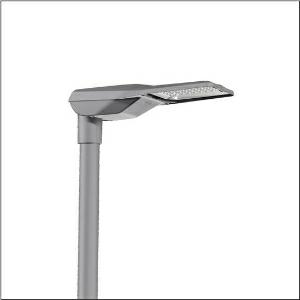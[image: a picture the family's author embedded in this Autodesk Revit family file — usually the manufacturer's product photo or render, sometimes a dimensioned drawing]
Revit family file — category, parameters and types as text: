
# Revit family: streetlight_sl_21_iq_mini___st0_8a_5xe2c41d08hb_7f29
name_source: partatom
category: Lighting Fixtures
units: mm (PartAtom-declared; Revit-internal decimal feet)

## family parameters
Cut with Voids When Loaded = No
Host = Face
Light Source = No
Part Type = Normal
Room Calculation Point = No
Round Connector Dimension = Use Diameter
Shared = No

## types (1)
- --- (1 x LED, 9860 lm, 70.9 W, 4000K)
    Apparent Load = 71 VA
    CIE Flux Codes = 38 75 97 100 100
    Color Rendering = 70
    Color Temperature = 4000K
    Default Elevation = 1800 mm
    Description = Streetlight SL 21 iQ mini, mast luminaire, primary light control with lens, of PMMA, primary optical cover: cover, of toughened safety glass, transparent, light distribution: ST0.8a, light emission: direct distribution, primary light characteristic: asymmetric, installation type: post-top, side-entry, LED, High Power LED, rated luminous flux: 9.860lm, luminous efficacy: 139lm/W, light colour: 740, colour temperature: 4000K, control gear: iQ-Comfort, control: Auto-Match, Temp-Guard, Lumen-Switch, Night-Set, Smart-Wire, Light-Fading, Desk-Remote (wireless, voltage-free reading and setting of iQ features in the workshop via application-optimized NFC function/RFID function), optimised constant luminous flux control (CLO 2.0), pre-setting: linear dimming characteristic, mains connection: 220..240V, AC, 50/60Hz, start of lifetime: 71W, end of service life: 75W, reduction: 31W, luminaire housing, of diecast aluminium, powder-coated, SITECO metallic grey (DB 702S), corrosivity category C5 high according to DIN EN ISO 12944, please order mast flange separately, inclination adjustable: 0°, 5°, 10°, 15°, sealing non-destructively replaceable, multi-level sealing system, length: 628mm, width: 235mm, height: 110mm, mast flange for spigot size: 42mm (side-entry): 5XC10008XM4, 60/48mm (side-entry/post-top): 5XC10108XM2, 76/60mm (side-entry/post-top): 5XC10108XM1, mounting height: 4..8m, protection rating (complete): IP66, insulation class (complete): insulation class II (safety insulation), certification: CE, ENEC, ENEC+, VDE, impact resistance: IK10, permissible operating ambient temperature for outdoor applications: -40..+50°C, standard-compliant lighting for roads and squares, packaging unit: 1 piece

Light Distribution: ST0.8a
    Height = 110 mm
    Lamp = 1 x LED
    Lamp Light Flux = 9860 lm
    Lamp Power = 70.9 W
    Lamp count = 1
    Length = 625 mm
    Luminous efficacy = 139 lm/W
    Manufacturer = Siteco
    ModVariant = No
    Model = 5XE2C41D08HB
    Number of Poles = 1
    OnlyDefault = Yes
    Power Factor = 1
    Product Name = Streetlight SL 21 iQ mini | ST0.8a
    Product group = mast luminaire | pylon top
    ProductGroupID = 6100
    Protection Class = Protection class II
    Protection Degree = IP 66
    RLX_Detail_Level = 1
    RLX_Emergency_Light_Flux = 0 lm
    RLX_Emergency_Type = 0
    RLX_Emergency_Type_DB = No
    RlxData = <blob elided: 26345 chars, md5=9a466215>
    Socket = socket
    Standby Power = 0 W
    System Light Flux = 9860 lm
    System Power = 71 W
    Type Comments = factory setting: luminous flux: 100 % | dim-lin: 254 | 711 mA
    Type Image = l_1003519.jpg
    URL = http://relux.com
    VarID = @adj_156843
    Voltage = 0 V
    Weight = 0.00 kg
    Width = 234 mm

## geometry (parser evidence)
native form markers: Blend x4, Sweep x9
no freeform markers — native parametric forms only
